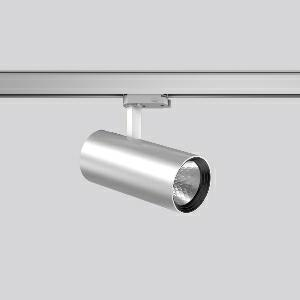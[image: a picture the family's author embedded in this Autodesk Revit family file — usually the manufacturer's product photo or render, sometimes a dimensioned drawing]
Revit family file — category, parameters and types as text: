
# Revit family: deecos_s_mini_742196_004_40d0
name_source: partatom
category: Lighting Fixtures
units: mm (PartAtom-declared; Revit-internal decimal feet)

## family parameters
Cut with Voids When Loaded = No
Host = Face
Light Source = No
Part Type = Normal
Room Calculation Point = No
Round Connector Dimension = Use Diameter
Shared = No

## types (1)
- DEECOS S mini (1 x LED Modul 930, 2450 lm, 3000)
    Apparent Load = 20 VA
    Approval mark = CE
    CIE Flux Codes = 99 100 100 100 100
    Color Rendering = 90
    Color Temperature = 3000
    Default Elevation = 1800 mm
    Description = Series: DEECOS S mini
LED surface-mounted projector in modern design with no visible cooling ribs. Housing: die-cast aluminium, powder-coated. Rotation range: 356°. Swivel range: 90°. Black plastic ring and recessed LED to prevent glare from the side. Optical assembly with reflector made of MIRO-Silver with 98% total light reflection for outstanding efficiency - can be changed without tools. Best colour rendering index Ra>90. With multi adaptor for 3-circuit tracks 230 V. Suitable for Track on ceiling, Wall track. High quality converter without flickering and stroboscopic effect. The following accessories can be mounted without use of tools: interchangeable lenses, decorative glasses, honeycomb louvre, clear and frosted diffusers, white interchangeable plastic ring. 
Colour: silver
Diameter: 87 mm
Height: 214 mm
Lamp: LED
Socket: without socket
Colour temperature: 3000K
Colour rendering index (CRI): 92
System power: 20 W
Rated luminous flux: 2450 lm
Luminous efficiency: 123 lm/W
Control gear: Regulated power supply
Protection class: I
Type of protection: IP 20
    Height = 214 mm
    Lamp = 1 x LED Modul 930
    Lamp Light Flux = 2450 lm
    Lamp count = 1
    Length = 87 mm
    Lifetime = 50000 h
    Luminous efficacy = 123 lm/W
    Manufacturer = RZB
    ModVariant = No
    Model = 742196.004
    Mounting Place = Ceiling
    Mounting Type = Rail mounted
    Number of Poles = 1
    OnlyDefault = Yes
    Power Factor = 1
    Product Name = DEECOS S mini
    Product group = Track mounted projectors
    ProductGroupID = 301
    Protection Class = Protection class I
    Protection Degree = IP 20
    RLX_Detail_Level = 1
    RLX_Emergency_Light_Flux = 0 lm
    RLX_Emergency_Type = 0
    RLX_Emergency_Type_DB = No
    RlxData = <blob elided: 37577 chars, md5=5b1d6da6>
    Socket = socket
    Standby Power = 0 W
    System Light Flux = 2450 lm
    System Power = 20 W
    Type Comments = Product without accessories
    Type Image = 741926.004.jpg
    URL = http://relux.com
    VarID = ---
    Voltage = 230 V
    Voltage Range = 220-240 V
    Weight = 0.00 kg
    Width = 0 mm  [stored 0 ft]

note: [stored X ft] marks values corroborated as IEEE doubles in the binary element streams (Revit-internal decimal feet)

## geometry (parser evidence)
native form markers: Blend x4, Sweep x13
no freeform markers — native parametric forms only
